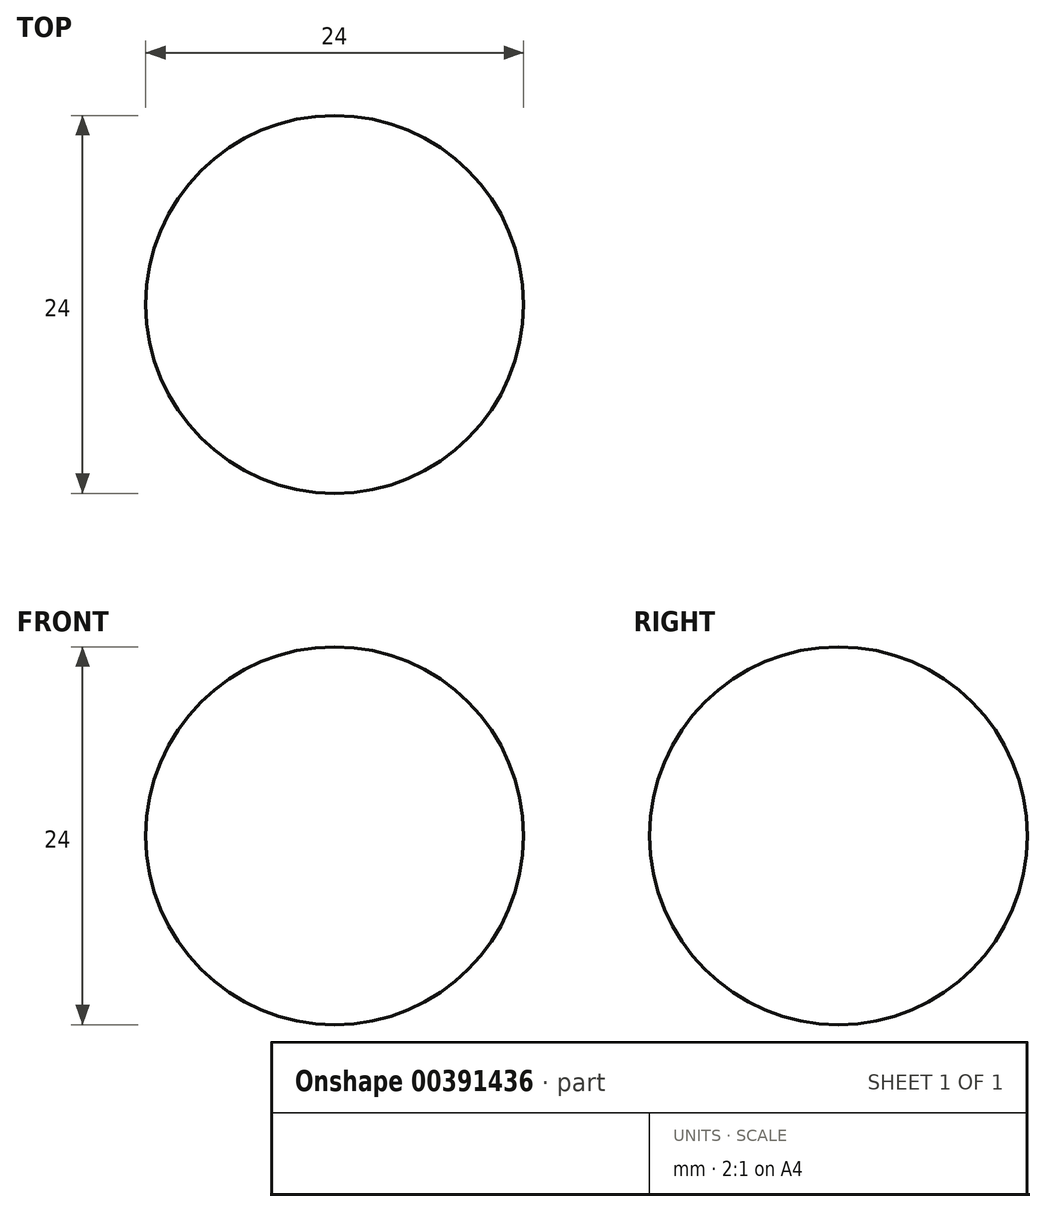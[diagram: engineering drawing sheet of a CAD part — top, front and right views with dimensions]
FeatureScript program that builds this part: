
annotation { "Feature Type Name" : "Feature", "Feature Type Description" : "" }
export const myFeature = defineFeature(function(context is Context, id is Id, definition is map)
    precondition{}
    {
        {
            var Q0;
            Q0=qCreatedBy(makeId("Front.planeOp"),FACE);
            var sketch = newSketch(context, id + "F0", { "sketchPlane" : qUnion([Q0])});
            skLineSegment(sketch, "E0", {"start": v(0, 12) * mm, "end": v(0, -12) * mm});
            skPoint(sketch, "E1", {"position": v(0, 0) * mm});
            skArc(sketch, "E2", {"start": v(0, 12) * mm, "mid": v(-12, 0) * mm, "end": v(0, -12) * mm});
            skSolve(sketch);
        }
        {
            var Q0;
            Q0=qSketchRegion(id+"F0",true);
            var Q1;
            Q1=sQuery(id+"F0.wireOp",EDGE,"E0");
            revolve(context, id + "F1", {"entities" : qUnion([Q0]), "axis" : qUnion([Q1]), "revolveType" : RevolveType.FULL});
        }
    });
